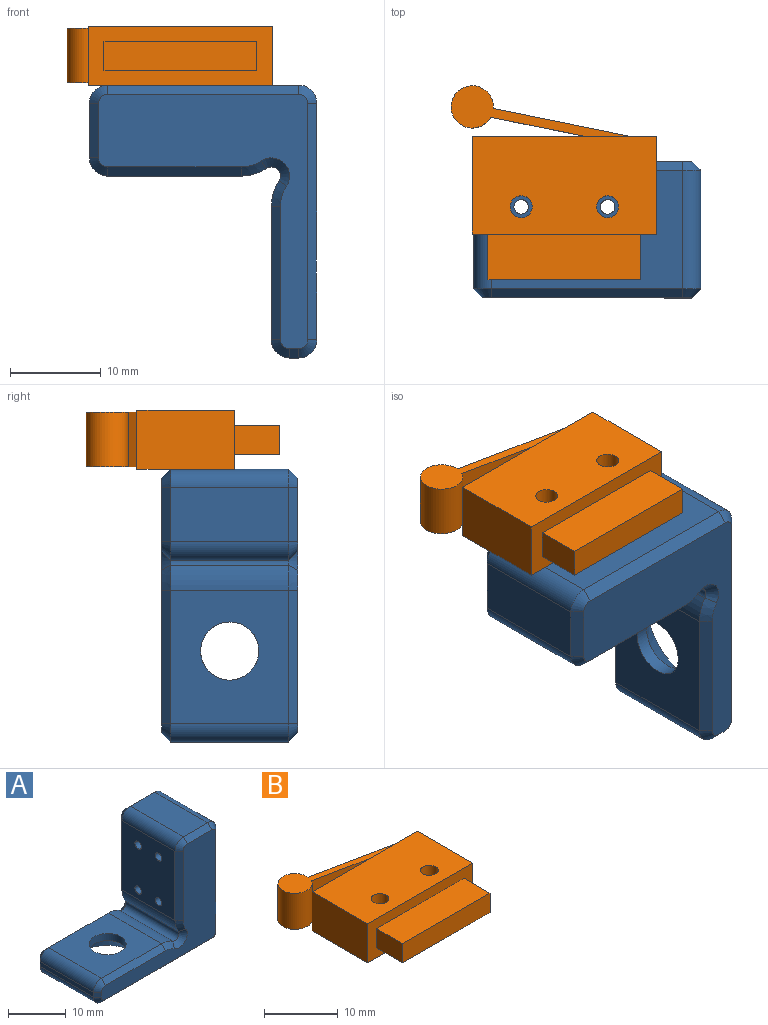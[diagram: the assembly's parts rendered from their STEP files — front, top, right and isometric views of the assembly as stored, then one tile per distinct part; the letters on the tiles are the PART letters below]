
ASSEMBLY  parts=2 mates=1
PART A: 51 faces, bbox 30x15x25 mm
  f0: plane 13x6.38mm, normal (0,0,-1), area 33.9mm2, adj f17,f19,f25,f39
  f1: plane 14.68x13mm, normal (0,0,1), area 158.7mm2, adj f14,f16,f18,f28,f42
  f2: plane 14.68x13mm, normal (-1,0,0), area 182.8mm2, adj f9,f10,f11,f12,f15,f22,f36,f50
  f3: plane 13x1mm, normal (-1,0,0), area 13mm2, adj f18,f19,f24,f38
  f4: plane 16.38x13mm, normal (0,0,-1), area 163.9mm2, adj f17,f20,f25,f39
  f5: plane 21x13mm, normal (1,0,0), area 265mm2, adj f9,f10,f11,f12,f20,f21,f29,f43
  f6: plane 13x6mm, normal (0,0,1), area 78mm2, adj f21,f22,f33,f47
  f7: plane 28x23mm, normal (0,-1,0), area 237.9mm2, adj f37,f38,f39,f40,f41,f42,f43,f44
  f8: plane 28x23mm, normal (0,1,0), area 237.9mm2, adj f23,f24,f25,f26,f27,f28,f29,f30
  f9: cylinder r=0.8mm len=10mm, axis (1,0,0), area 50.3mm2, adj f2,f5
  f10: cylinder r=0.8mm len=10mm, axis (1,0,0), area 50.3mm2, adj f2,f5
  f11: cylinder r=0.8mm len=10mm, axis (1,0,0), area 50.3mm2, adj f2,f5
  f12: cylinder r=0.8mm len=10mm, axis (1,0,0), area 50.3mm2, adj f2,f5
  f13: cylinder r=1mm len=13mm, axis (0,1,0), area 35.6mm2, adj f14,f15,f32,f46
  f14: cylinder r=5mm len=13mm, axis (0,1,0), area 38.1mm2, adj f1,f13,f30,f44
  f15: cylinder r=5mm len=13mm, axis (0,1,0), area 38.1mm2, adj f2,f13,f34,f48
  f16: cylinder r=3.2mm len=6.4mm, axis (0,0,1), area 30.2mm2, adj f1,f17
  f17: cone r=3.2mm half-angle=45deg, axis (0,0,-1), area 153.3mm2, adj f0,f4,f16,f25,f39
  f18: cylinder r=2mm len=13mm, axis (0,1,0), area 40.8mm2, adj f1,f3,f26,f40
  f19: cylinder r=2mm len=13mm, axis (0,1,0), area 40.8mm2, adj f0,f3,f23,f37
  f20: cylinder r=2mm len=13mm, axis (0,1,0), area 40.8mm2, adj f4,f5,f27,f41
  f21: cylinder r=2mm len=13mm, axis (0,1,0), area 40.8mm2, adj f5,f6,f31,f45
  f22: cylinder r=2mm len=13mm, axis (0,1,0), area 40.8mm2, adj f2,f6,f35,f49
  f23: cone r=1mm half-angle=45deg, axis (0,-1,0), area 3.3mm2, adj f8,f19,f24,f25
  f24: plane 1x1mm, normal (-0.71,0.71,0), area 1.4mm2, adj f3,f8,f23,f26
  f25: plane 26x1mm, normal (0,0.71,-0.71), area 36.5mm2, adj f0,f4,f8,f17,f23,f27
  f26: cone r=1mm half-angle=45deg, axis (0,-1,0), area 3.3mm2, adj f8,f18,f24,f28
  f27: cone r=1mm half-angle=45deg, axis (0,-1,0), area 3.3mm2, adj f8,f20,f25,f29
  f28: plane 14.68x1mm, normal (0,0.71,0.71), area 20.8mm2, adj f1,f8,f26,f30
  f29: plane 21x1mm, normal (0.71,0.71,0), area 29.7mm2, adj f5,f8,f27,f31
  f30: cone r=4mm half-angle=45deg, axis (0,-1,0), area 3.7mm2, adj f8,f14,f28,f32
  f31: cone r=1mm half-angle=45deg, axis (0,-1,0), area 3.3mm2, adj f8,f21,f29,f33
  f32: cone r=1mm half-angle=45deg, axis (0,1,0), area 5.8mm2, adj f8,f13,f30,f34
  f33: plane 6x1mm, normal (0,0.71,0.71), area 8.5mm2, adj f6,f8,f31,f35
  f34: cone r=4mm half-angle=45deg, axis (0,-1,0), area 3.7mm2, adj f8,f15,f32,f36
  f35: cone r=1mm half-angle=45deg, axis (0,-1,0), area 3.3mm2, adj f8,f22,f33,f36
  f36: plane 14.68x1mm, normal (-0.71,0.71,0), area 20.8mm2, adj f2,f8,f34,f35
  f37: cone r=1mm half-angle=45deg, axis (0,1,0), area 3.3mm2, adj f7,f19,f38,f39
  f38: plane 1x1mm, normal (-0.71,-0.71,0), area 1.4mm2, adj f3,f7,f37,f40
  f39: plane 26x1mm, normal (0,-0.71,-0.71), area 36.5mm2, adj f0,f4,f7,f17,f37,f41
  f40: cone r=1mm half-angle=45deg, axis (0,1,0), area 3.3mm2, adj f7,f18,f38,f42
  f41: cone r=1mm half-angle=45deg, axis (0,1,0), area 3.3mm2, adj f7,f20,f39,f43
  f42: plane 14.68x1mm, normal (0,-0.71,0.71), area 20.8mm2, adj f1,f7,f40,f44
  f43: plane 21x1mm, normal (0.71,-0.71,0), area 29.7mm2, adj f5,f7,f41,f45
  f44: cone r=4mm half-angle=45deg, axis (0,1,0), area 3.7mm2, adj f7,f14,f42,f46
  f45: cone r=1mm half-angle=45deg, axis (0,1,0), area 3.3mm2, adj f7,f21,f43,f47
  f46: cone r=2mm half-angle=45deg, axis (0,-1,0), area 5.8mm2, adj f7,f13,f44,f48
  f47: plane 6x1mm, normal (0,-0.71,0.71), area 8.5mm2, adj f6,f7,f45,f49
  f48: cone r=4mm half-angle=45deg, axis (0,1,0), area 3.7mm2, adj f7,f15,f46,f50
  f49: cone r=1mm half-angle=45deg, axis (0,1,0), area 3.3mm2, adj f7,f22,f47,f50
  f50: plane 14.68x1mm, normal (-0.71,-0.71,0), area 20.8mm2, adj f2,f7,f48,f49
PART B: 18 faces, bbox 22.6x21.3x6.5 mm
  f0: plane 20.25x6.5mm, normal (0,-1,0), area 77.9mm2, adj f1,f5,f6,f7,f8,f9,f11,f12
  f1: plane 10.7x6.5mm, normal (1,0,0), area 69.5mm2, adj f0,f2,f6,f7
  f2: plane 20.25x6.5mm, normal (0,1,0), area 101.6mm2, adj f1,f5,f6,f7,f14,f15,f16,f17
  f3: cylinder r=1.2mm len=6.5mm, axis (0,0,-1), area 49mm2, adj f6,f7
  f4: cylinder r=1.2mm len=6.5mm, axis (0,0,-1), area 49mm2, adj f6,f7
  f5: plane 10.7x6.5mm, normal (-1,0,0), area 69.5mm2, adj f0,f2,f6,f7
  f6: plane 20.25x10.7mm, normal (0,0,1), area 207.6mm2, adj f0,f1,f2,f3,f4,f5
  f7: plane 20.25x10.7mm, normal (0,0,-1), area 207.6mm2, adj f0,f1,f2,f3,f4,f5
  f8: plane 5x3.2mm, normal (1,0,0), area 16mm2, adj f0,f10,f11,f12
  f9: plane 5x3.2mm, normal (-1,0,0), area 16mm2, adj f0,f10,f11,f12
  f10: plane 16.8x3.2mm, normal (0,-1,0), area 53.8mm2, adj f8,f9,f11,f12
  f11: plane 16.8x5mm, normal (0,0,1), area 84mm2, adj f0,f8,f9,f10
  f12: plane 16.8x5mm, normal (0,0,-1), area 84mm2, adj f0,f8,f9,f10
  f13: cylinder r=2.32mm len=6mm, axis (0,0,-1), area 81.6mm2, adj f14,f15,f16,f17
  f14: plane 10.51x6mm, normal (-0.2,-0.98,0), area 64.3mm2, adj f2,f13,f16,f17
  f15: plane 15.22x6mm, normal (0.2,0.98,0), area 93.2mm2, adj f2,f13,f16,f17
  f16: plane 19.87x5.6mm, normal (0,0,1), area 30.1mm2, adj f2,f13,f14,f15
  f17: plane 19.87x5.6mm, normal (0,0,-1), area 30.1mm2, adj f2,f13,f14,f15
PLACE A rot(axis=(0,-1,0),90deg) t=(0,-4.85,-23.25)mm
PLACE B at identity fixed
MATE fastened B.f3 <-> A.f9  axis (0,0,-1) through (-4.75,-2.35,-3.25)mm
